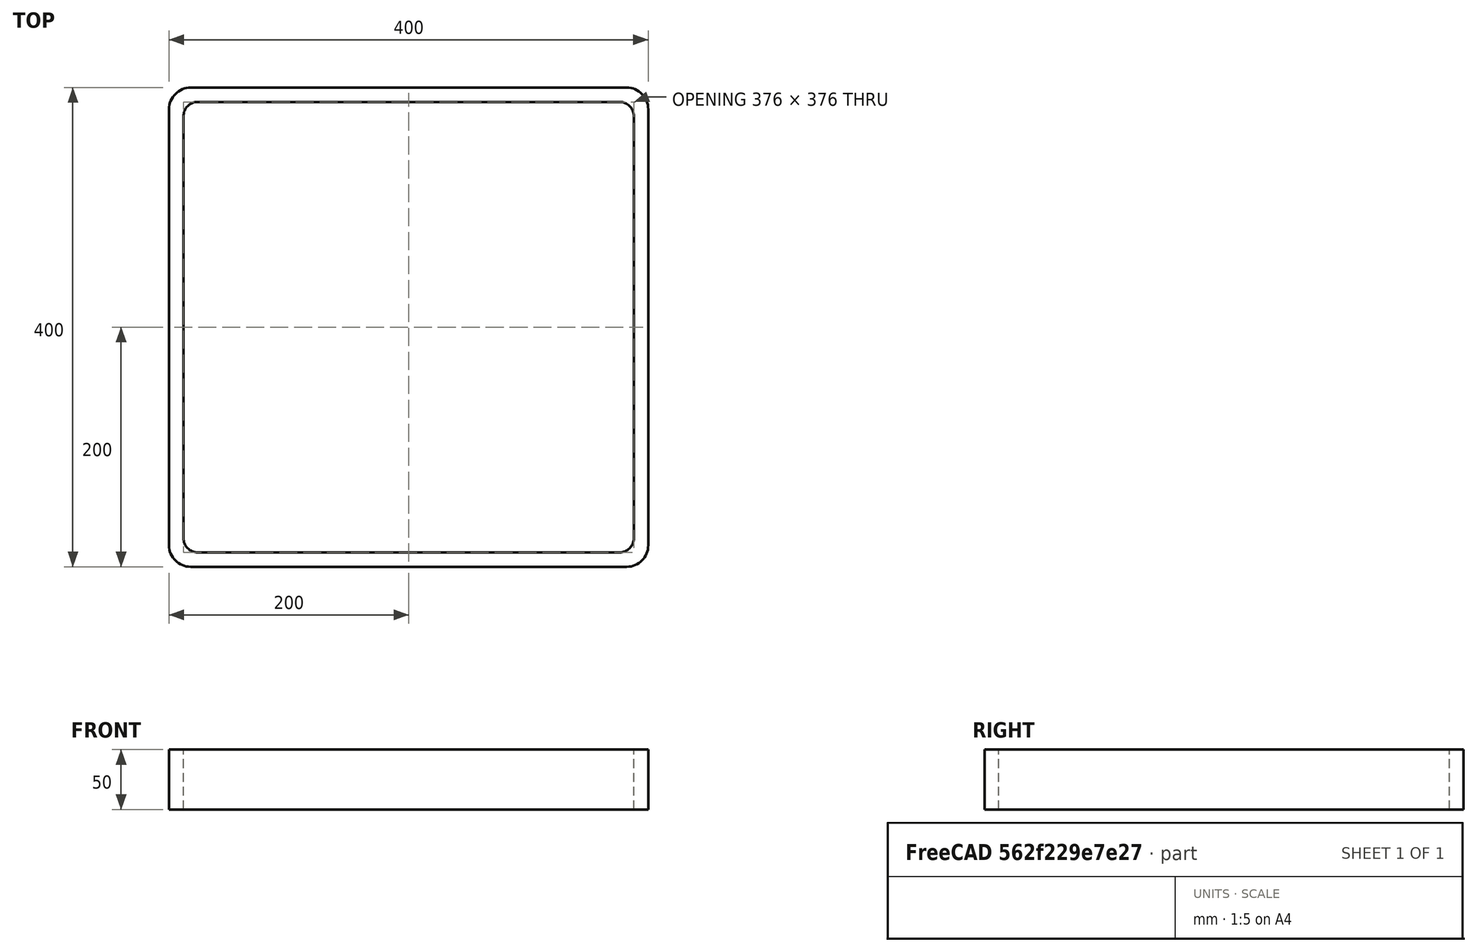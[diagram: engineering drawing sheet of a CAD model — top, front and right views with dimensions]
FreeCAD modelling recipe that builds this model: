
FCSTD DOCUMENT  (FreeCAD 0.15R4671 (Git))
Label: Square hollow section 400x400x12 EN10219 S235JRH
License: All rights reserved
LicenseURL: http://en.wikipedia.org/wiki/All_rights_reserved
objects: Sketcher::SketchObject×1, Part::Extrusion×1
note: 2 computed .brp shape members not serialized (recipe doc carries the construction recipe); baked Part::Feature solids carry a one-line shape summary decoded from their .brp

FEATURE [Sketcher::SketchObject] Sketch
  sketch-geometry (16):
    g0: LineSegment StartX=-176 StartY=188 StartZ=0 EndX=176 EndY=188 EndZ=0
    g1: LineSegment StartX=188 StartY=176 StartZ=0 EndX=188 EndY=-176 EndZ=0
    g2: LineSegment StartX=176 StartY=-188 StartZ=0 EndX=-176 EndY=-188 EndZ=0
    g3: LineSegment StartX=-188 StartY=-176 StartZ=0 EndX=-188 EndY=176 EndZ=0
    g4: LineSegment StartX=-182 StartY=200 StartZ=0 EndX=182 EndY=200 EndZ=0
    g5: LineSegment StartX=200 StartY=182 StartZ=0 EndX=200 EndY=-182 EndZ=0
    g6: LineSegment StartX=182 StartY=-200 StartZ=0 EndX=-182 EndY=-200 EndZ=0
    g7: LineSegment StartX=-200 StartY=-182 StartZ=0 EndX=-200 EndY=182 EndZ=0
    g8: ArcOfCircle CenterX=-176 CenterY=176 CenterZ=0 NormalX=0 NormalY=0 NormalZ=1 Radius=12 StartAngle=1.5708 EndAngle=3.14159
    g9: ArcOfCircle CenterX=176 CenterY=176 CenterZ=0 NormalX=0 NormalY=0 NormalZ=1 Radius=12 StartAngle=0 EndAngle=1.5708
    g10: ArcOfCircle CenterX=176 CenterY=-176 CenterZ=0 NormalX=0 NormalY=0 NormalZ=1 Radius=12 StartAngle=4.71239 EndAngle=6.28319
    g11: ArcOfCircle CenterX=-176 CenterY=-176 CenterZ=0 NormalX=0 NormalY=0 NormalZ=1 Radius=12 StartAngle=3.14159 EndAngle=4.71239
    g12: ArcOfCircle CenterX=182 CenterY=182 CenterZ=0 NormalX=0 NormalY=0 NormalZ=1 Radius=18 StartAngle=0 EndAngle=1.5708
    g13: ArcOfCircle CenterX=182 CenterY=-182 CenterZ=0 NormalX=0 NormalY=0 NormalZ=1 Radius=18 StartAngle=4.71239 EndAngle=6.28319
    g14: ArcOfCircle CenterX=-182 CenterY=-182 CenterZ=0 NormalX=0 NormalY=0 NormalZ=1 Radius=18 StartAngle=3.14159 EndAngle=4.71239
    g15: ArcOfCircle CenterX=-182 CenterY=182 CenterZ=0 NormalX=0 NormalY=0 NormalZ=1 Radius=18 StartAngle=1.5708 EndAngle=3.14159
  constraints (36):
    c: Horizontal(g2)
    c: Vertical(g3)
    c: Horizontal(g6)
    c: Vertical(g7)
    c: Tangent(g3,g8) = 1.5708
    c: Tangent(g0,g8) = 1.5708
    c: Tangent(g0,g9) = 1.5708
    c: Tangent(g1,g9) = 1.5708
    c: Tangent(g1,g10) = 1.5708
    c: Tangent(g2,g10) = 1.5708
    c: Tangent(g2,g11) = 1.5708
    c: Tangent(g3,g11) = 1.5708
    c: Tangent(g4,g12) = 1.5708
    c: Tangent(g5,g12) = 1.5708
    c: Tangent(g5,g13) = 1.5708
    c: Tangent(g6,g13) = 1.5708
    c: Tangent(g6,g14) = 1.5708
    c: Tangent(g7,g14) = 1.5708
    c: Tangent(g7,g15) = 1.5708
    c: Tangent(g4,g15) = 1.5708
    c: Equal(g9,g8)
    c: Equal(g9,g11)
    c: Equal(g9,g10)
    c: Equal(g12,g15)
    c: Equal(g12,g14)
    c: Equal(g12,g13)
    c: Symmetric(g4,g6,g-1)
    c: Symmetric(g7,g5,g-2)
    c: DistanceY(g4,g6) = -400
    c: DistanceX(g7,g5) = 400
    c: Symmetric(g3,g1,g-2)
    c: Symmetric(g0,g2,g-1)
    c: DistanceY(g0,g4) = 12
    c: DistanceX(g5,g1) = -12
    c: Radius(g9) = 12
    c: Radius(g12) = 18
FEATURE [Part::Extrusion] Extrude  label="Square hollow section 400x400x12 EN10219 S235JRH"
  Base = -> Sketch
  Dir = (0,0,50)
  Solid = true
